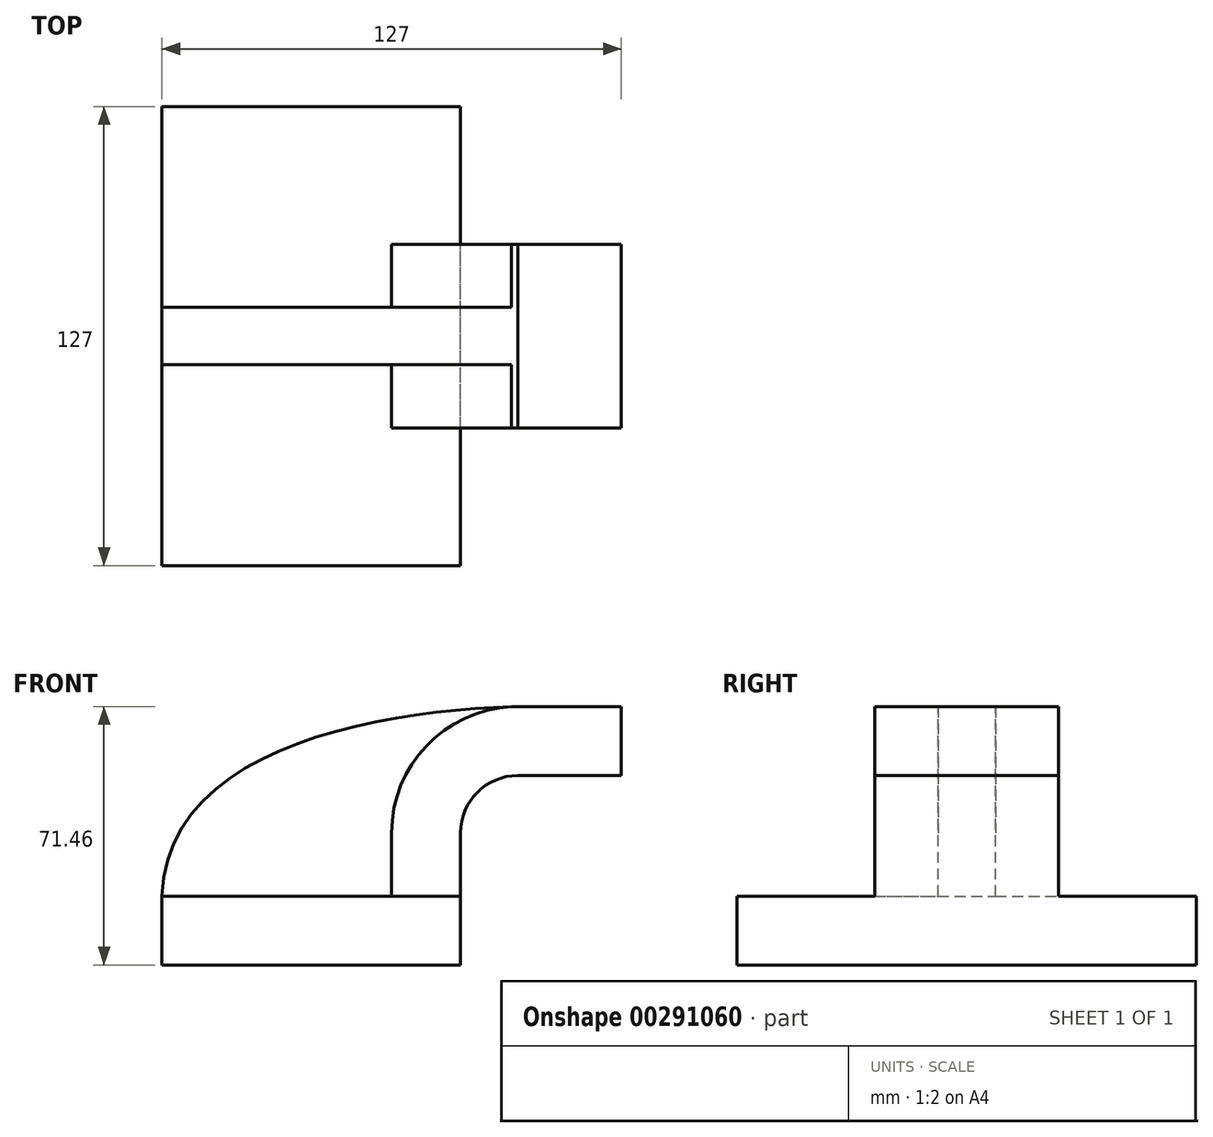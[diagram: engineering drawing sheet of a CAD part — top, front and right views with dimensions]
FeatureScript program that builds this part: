
annotation { "Feature Type Name" : "Feature", "Feature Type Description" : "" }
export const myFeature = defineFeature(function(context is Context, id is Id, definition is map)
    precondition{}
    {
        {
            var Q0;
            Q0=qCreatedBy(makeId("Front.planeOp"),FACE);
            var sketch = newSketch(context, id + "F0", { "sketchPlane" : qUnion([Q0])});
            skLineSegment(sketch, "E0.bottom", {"start": v(41.28, 9.53) * mm, "end": v(-41.28, 9.53) * mm});
            skLineSegment(sketch, "E0.top", {"start": v(41.27, -9.53) * mm, "end": v(-41.27, -9.53) * mm});
            skLineSegment(sketch, "E0.left", {"start": v(41.28, 9.52) * mm, "end": v(41.28, -9.53) * mm});
            skLineSegment(sketch, "E0.right", {"start": v(-41.28, 9.53) * mm, "end": v(-41.28, -9.53) * mm});
            skPoint(sketch, "E0.middle", {"position": v(0, 0) * mm});
            skLineSegment(sketch, "E1.bottom", {"start": v(60.33, 38.1) * mm, "end": v(111.13, 38.1) * mm});
            skLineSegment(sketch, "E1.top", {"start": v(60.33, 66.67) * mm, "end": v(111.13, 66.67) * mm});
            skLineSegment(sketch, "E1.left", {"start": v(60.33, 38.1) * mm, "end": v(60.33, 66.68) * mm});
            skLineSegment(sketch, "E1.right", {"start": v(111.13, 38.1) * mm, "end": v(111.13, 66.68) * mm});
            skPoint(sketch, "E1.middle", {"position": v(85.73, 52.39) * mm});
            skLineSegment(sketch, "E2", {"start": v(41.28, 9.53) * mm, "end": v(41.28, 27) * mm});
            skArc(sketch, "E3", {"start": v(41.28, 27) * mm, "mid": v(45.92, 38.23) * mm, "end": v(57.15, 42.88) * mm});
            skLineSegment(sketch, "E4", {"start": v(57.15, 42.88) * mm, "end": v(85.73, 42.88) * mm});
            skLineSegment(sketch, "E5.0", {"start": v(57.15, 61.93) * mm, "end": v(85.73, 61.93) * mm});
            skArc(sketch, "E5.1", {"start": v(22.23, 27) * mm, "mid": v(32.45, 51.7) * mm, "end": v(57.15, 61.93) * mm});
            skLineSegment(sketch, "E5.2", {"start": v(22.23, 9.53) * mm, "end": v(22.23, 27) * mm});
            skLineSegment(sketch, "E6", {"start": v(85.73, 38.1) * mm, "end": v(85.73, 66.67) * mm});
            skFitSpline(sketch, "E7", {"points": [v(-41.28, 9.52) * mm, v(57.15, 61.93) * mm], "startDerivative": vector(3.57, 125.29) * mm, "endDerivative": vector(110.51, 2.44) * mm});
            skSolve(sketch);
        }
        {
            var Q0;
            Q0=makeQuery(id+"F0.imprint","IMPRINT",FACE,{"disambiguationData":[TD([[makeQuery(id+"F0.imprint","IMPRINT",EDGE,{"derivedFrom":sQuery(id+"F0.wireOp",EDGE,"E0.top")}),-1.0]])]});
            extrude(context, id + "F1", {"entities" : qUnion([Q0]), "endBound" : BoundingType.SYMMETRIC, "depth" : 127 * mm});
        }
        {
            var Q0;
            {var subQ1=sQuery(id+"F0.wireOp",EDGE,"E2");Q0=makeQuery(id+"F0.imprint","IMPRINT",FACE,{"disambiguationData":[TD([[makeQuery(id+"F0.imprint","IMPRINT",EDGE,{"derivedFrom":subQ1}),1.0]])]});}
            var Q1;
            {var subQ0=sQuery(id+"F0.wireOp",EDGE,"E4");var subQ1=sQuery(id+"F0.wireOp",EDGE,"E1.left");var subQ2=makeQuery(id+"F0.imprint","INTERSECT",VERTEX,{"derivedFrom":[subQ1,subQ0]});Q1=makeQuery(id+"F0.imprint","IMPRINT",FACE,{"disambiguationData":[TD([[makeQuery(id+"F0.imprint","IMPRINT",EDGE,{"disambiguationData":[TD([[subQ2,-1.0]])],"derivedFrom":subQ1}),-1.0]])]});}
            extrude(context, id + "F2", {"entities" : qUnion([Q0, Q1]), "operationType" : NewBodyOperationType.ADD, "endBound" : BoundingType.SYMMETRIC, "depth" : 50.8 * mm});
        }
        {
            var Q0;
            {var subQ3=sQuery(id+"F0.wireOp",EDGE,"E5.2");Q0=makeQuery(id+"F0.imprint","IMPRINT",FACE,{"disambiguationData":[TD([[makeQuery(id+"F0.imprint","IMPRINT",EDGE,{"derivedFrom":subQ3}),1.0]])]});}
            extrude(context, id + "F3", {"entities" : qUnion([Q0]), "operationType" : NewBodyOperationType.ADD, "endBound" : BoundingType.SYMMETRIC, "depth" : 15.88 * mm});
        }
    });
